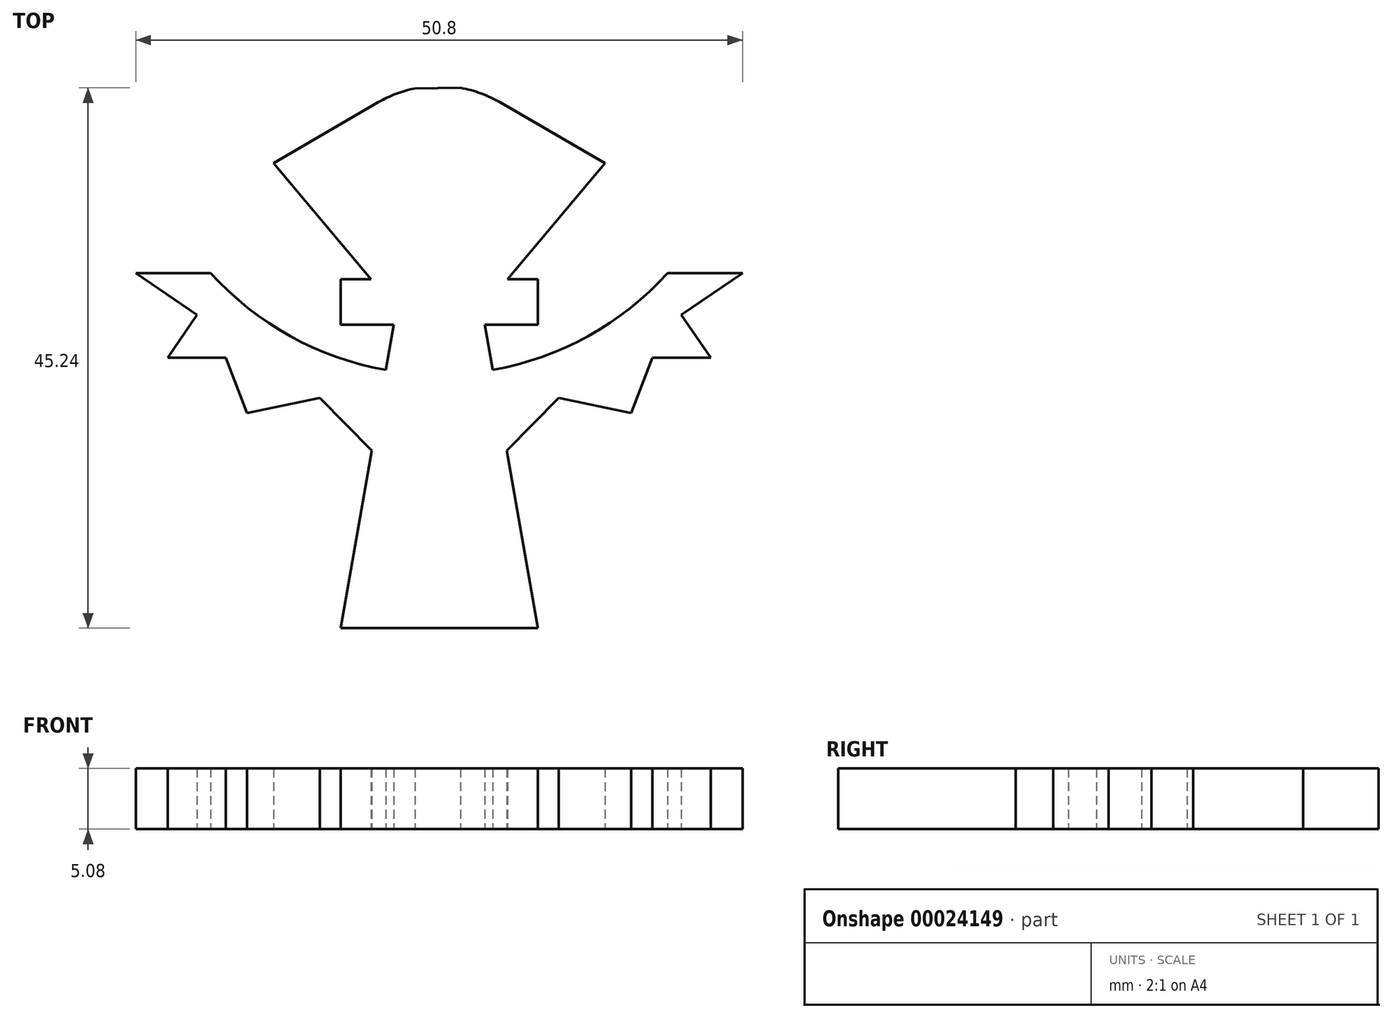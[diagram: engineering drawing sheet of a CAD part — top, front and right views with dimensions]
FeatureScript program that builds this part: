
annotation { "Feature Type Name" : "Feature", "Feature Type Description" : "" }
export const myFeature = defineFeature(function(context is Context, id is Id, definition is map)
    precondition{}
    {
        {
            var Q0;
            Q0=qCreatedBy(makeId("Top.planeOp"),FACE);
            var sketch = newSketch(context, id + "F0", { "sketchPlane" : qUnion([Q0])});
            skLineSegment(sketch, "E0", {"start": v(-7.37, -28.72) * mm, "end": v(9.14, -28.72) * mm});
            skLineSegment(sketch, "E1", {"start": v(0.89, -28.72) * mm, "end": v(0.89, -3.32) * mm});
            skLineSegment(sketch, "E2", {"start": v(0.89, -3.32) * mm, "end": v(4.7, -3.32) * mm});
            skLineSegment(sketch, "E3", {"start": v(0.89, -3.32) * mm, "end": v(-2.92, -3.32) * mm});
            skLineSegment(sketch, "E4", {"start": v(-2.92, -3.32) * mm, "end": v(-7.37, -28.72) * mm});
            skLineSegment(sketch, "E5", {"start": v(4.7, -3.32) * mm, "end": v(9.14, -28.72) * mm});
            skLineSegment(sketch, "E6.bottom", {"start": v(-7.37, -3.32) * mm, "end": v(9.14, -3.32) * mm});
            skLineSegment(sketch, "E6.top", {"start": v(-7.37, 0.49) * mm, "end": v(9.14, 0.49) * mm});
            skLineSegment(sketch, "E6.left", {"start": v(-7.37, -3.32) * mm, "end": v(-7.37, 0.49) * mm});
            skLineSegment(sketch, "E6.right", {"start": v(9.14, -3.32) * mm, "end": v(9.14, 0.49) * mm});
            skPoint(sketch, "E7", {"position": v(-4.83, 0.49) * mm});
            skPoint(sketch, "E8", {"position": v(6.6, 0.49) * mm});
            skLineSegment(sketch, "E9", {"start": v(0.89, 0.49) * mm, "end": v(0.89, 18.27) * mm});
            skLineSegment(sketch, "E10", {"start": v(-4.83, 0.49) * mm, "end": v(-13, 10.22) * mm});
            skLineSegment(sketch, "E11", {"start": v(-13, 10.22) * mm, "end": v(-4.21, 15.31) * mm});
            skLineSegment(sketch, "E12.MirrorCS", {"start": v(6.6, 0.49) * mm, "end": v(14.76, 10.22) * mm});
            skLineSegment(sketch, "E13.MirrorCS", {"start": v(14.76, 10.22) * mm, "end": v(5.98, 15.31) * mm});
            skArc(sketch, "E14", {"start": v(-18.24, 1.02) * mm, "mid": v(-11.6, -4.26) * mm, "end": v(-3.58, -7.1) * mm});
            skLineSegment(sketch, "E15", {"start": v(-18.24, 1.02) * mm, "end": v(-24.51, 1.02) * mm});
            skArc(sketch, "E16.MirrorCS", {"start": v(20.01, 1.02) * mm, "mid": v(13.36, -4.26) * mm, "end": v(5.36, -7.1) * mm});
            skLineSegment(sketch, "E17.MirrorCS", {"start": v(20.01, 1.02) * mm, "end": v(26.29, 1.02) * mm});
            skLineSegment(sketch, "E18", {"start": v(-24.51, 1.02) * mm, "end": v(-19.39, -2.47) * mm});
            skLineSegment(sketch, "E19", {"start": v(-19.39, -2.47) * mm, "end": v(-21.85, -6.08) * mm});
            skLineSegment(sketch, "E20", {"start": v(-21.85, -6.08) * mm, "end": v(-16.98, -6.08) * mm});
            skLineSegment(sketch, "E21", {"start": v(-16.98, -6.08) * mm, "end": v(-15.2, -10.72) * mm});
            skLineSegment(sketch, "E22", {"start": v(-15.2, -10.72) * mm, "end": v(-9.11, -9.45) * mm});
            skLineSegment(sketch, "E23", {"start": v(-9.11, -9.45) * mm, "end": v(-4.77, -13.85) * mm});
            skLineSegment(sketch, "E24.MirrorCS", {"start": v(10.88, -9.45) * mm, "end": v(6.54, -13.85) * mm});
            skLineSegment(sketch, "E25.MirrorCS", {"start": v(16.97, -10.72) * mm, "end": v(10.88, -9.45) * mm});
            skLineSegment(sketch, "E26.MirrorCS", {"start": v(18.75, -6.08) * mm, "end": v(16.97, -10.72) * mm});
            skLineSegment(sketch, "E27.MirrorCS", {"start": v(23.62, -6.08) * mm, "end": v(18.75, -6.08) * mm});
            skLineSegment(sketch, "E28.MirrorCS", {"start": v(21.16, -2.47) * mm, "end": v(23.62, -6.08) * mm});
            skLineSegment(sketch, "E29.MirrorCS", {"start": v(26.29, 1.02) * mm, "end": v(21.16, -2.47) * mm});
            skArc(sketch, "E30.filletArc", {"start": v(5.98, 15.31) * mm, "mid": v(4.39, 16.06) * mm, "end": v(2.68, 16.52) * mm});
            skPoint(sketch, "E31", {"position": v(-1.12, 16.48) * mm});
            skPoint(sketch, "E32", {"position": v(2.68, 16.52) * mm});
            skArc(sketch, "E33.trimOffspring", {"start": v(-1.12, 16.48) * mm, "mid": v(-2.72, 16.02) * mm, "end": v(-4.21, 15.31) * mm});
            skLineSegment(sketch, "E34", {"start": v(-1.12, 16.48) * mm, "end": v(2.68, 16.52) * mm});
            skSolve(sketch);
        }
        {
            var Q0;
            Q0 = qSketchRegion(id + "F0", true);
            extrude(context, id + "F1", {"entities" : qUnion([Q0]), "depth" : 5.08 * mm});
        }
    });
